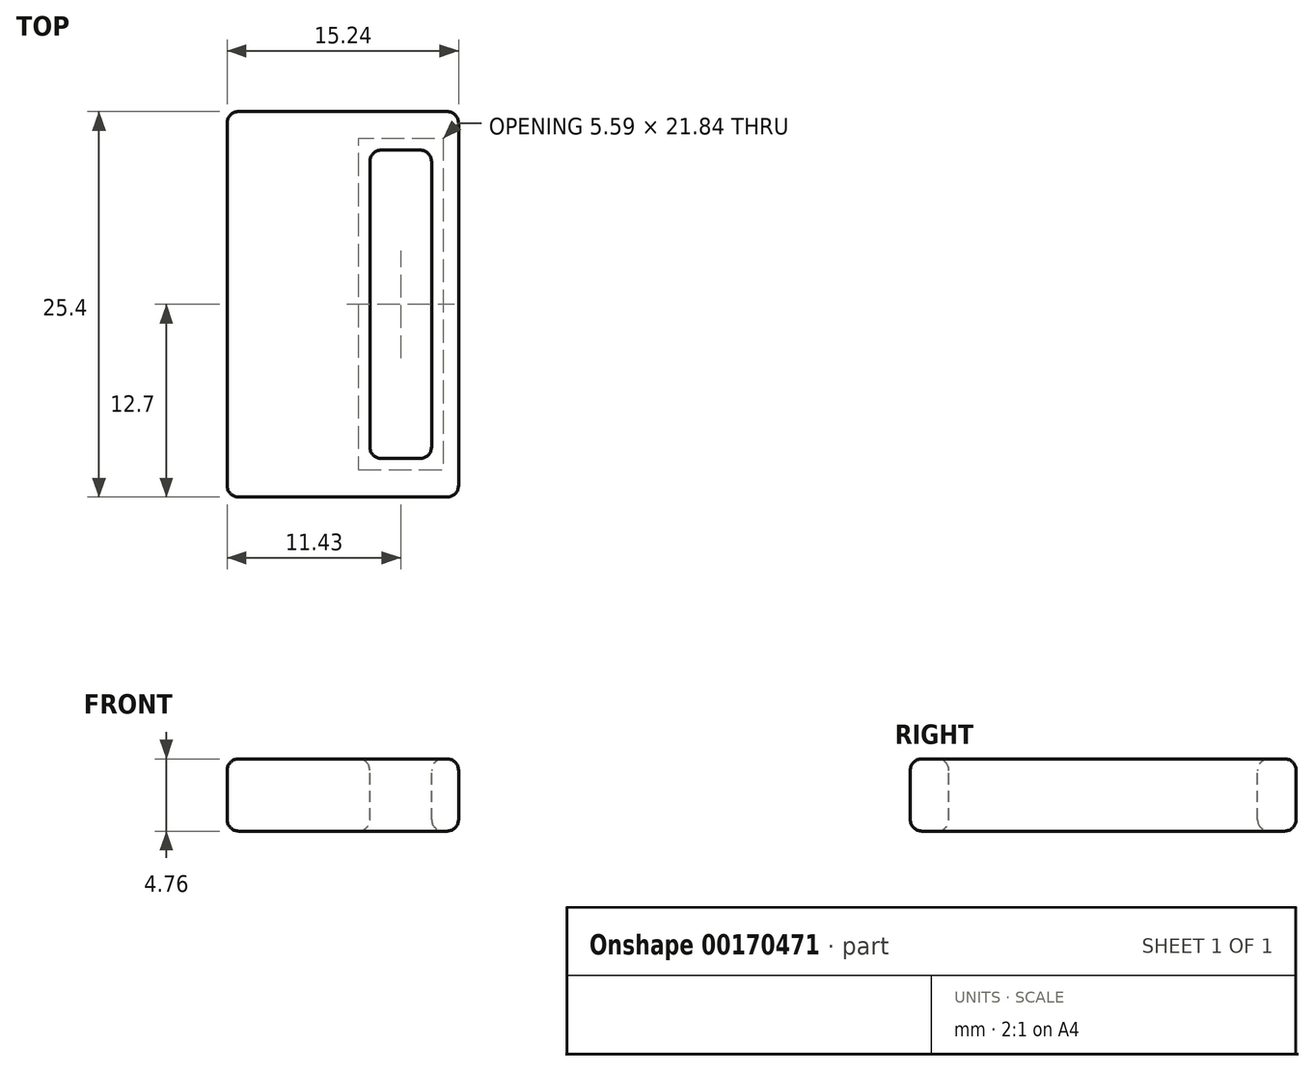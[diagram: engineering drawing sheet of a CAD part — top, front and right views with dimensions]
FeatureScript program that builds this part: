
annotation { "Feature Type Name" : "Feature", "Feature Type Description" : "" }
export const myFeature = defineFeature(function(context is Context, id is Id, definition is map)
    precondition{}
    {
        {
            var Q0;
            Q0=qCreatedBy(makeId("Top.planeOp"),FACE);
            var sketch = newSketch(context, id + "F0", { "sketchPlane" : qUnion([Q0])});
            skLineSegment(sketch, "E0.bottom", {"start": v(7.62, -12.7) * mm, "end": v(-7.62, -12.7) * mm});
            skLineSegment(sketch, "E0.top", {"start": v(7.62, 12.7) * mm, "end": v(-7.62, 12.7) * mm});
            skLineSegment(sketch, "E0.left", {"start": v(7.62, -12.7) * mm, "end": v(7.62, 12.7) * mm});
            skLineSegment(sketch, "E0.right", {"start": v(-7.62, -12.7) * mm, "end": v(-7.62, 12.7) * mm});
            skPoint(sketch, "E0.middle", {"position": v(0, 0) * mm});
            skSolve(sketch);
        }
        {
            var Q0;
            Q0=makeQuery(id+"F0.imprint","IMPRINT",FACE,{"disambiguationData":[TD([[makeQuery(id+"F0.imprint","IMPRINT",EDGE,{"derivedFrom":sQuery(id+"F0.wireOp",EDGE,"E0.bottom")}),-1.0]])]});
            extrude(context, id + "F1", {"entities" : qUnion([Q0]), "depth" : 4.76 * mm});
        }
        {
            var Q0;
            Q0=makeQuery(id+"F1.opExtrude","CAP_FACE",FACE,{"disambiguationData":[OSD([sQuery(id+"F0.wireOp",EDGE,"E0.bottom"),sQuery(id+"F0.wireOp",EDGE,"E0.top"),sQuery(id+"F0.wireOp",EDGE,"E0.left"),sQuery(id+"F0.wireOp",EDGE,"E0.right")])],"isStart":false});
            var sketch = newSketch(context, id + "F2", { "sketchPlane" : qUnion([Q0])});
            skLineSegment(sketch, "E1.bottom", {"start": v(5.84, -10.16) * mm, "end": v(1.78, -10.16) * mm});
            skLineSegment(sketch, "E1.top", {"start": v(5.84, 10.16) * mm, "end": v(1.78, 10.16) * mm});
            skLineSegment(sketch, "E1.left", {"start": v(5.84, -10.16) * mm, "end": v(5.84, 10.16) * mm});
            skLineSegment(sketch, "E1.right", {"start": v(1.78, -10.16) * mm, "end": v(1.78, 10.16) * mm});
            skPoint(sketch, "E1.middle", {"position": v(3.8, 0) * mm});
            skLineSegment(sketch, "E2", {"start": v(0, 0) * mm, "end": v(3.8, 0) * mm, "construction": true});
            skSolve(sketch);
        }
        {
            var Q0;
            Q0=makeQuery(id+"F2.imprint","IMPRINT",FACE,{"disambiguationData":[TD([[makeQuery(id+"F2.imprint","IMPRINT",EDGE,{"derivedFrom":sQuery(id+"F2.wireOp",EDGE,"E1.bottom")}),-1.0]])]});
            extrude(context, id + "F3", {"entities" : qUnion([Q0]), "operationType" : NewBodyOperationType.REMOVE, "oppositeDirection" : true, "depth" : 25.4 * mm});
        }
        {
            var Q0;
            Q0=makeQuery(id+"F1.opExtrude","CAP_FACE",FACE,{"disambiguationData":[OSD([sQuery(id+"F0.wireOp",EDGE,"E0.bottom"),sQuery(id+"F0.wireOp",EDGE,"E0.top"),sQuery(id+"F0.wireOp",EDGE,"E0.left"),sQuery(id+"F0.wireOp",EDGE,"E0.right")])],"isStart":false});
            var Q1;
            Q1=makeQuery(id+"F1.opExtrude","CAP_FACE",FACE,{"disambiguationData":[OSD([sQuery(id+"F0.wireOp",EDGE,"E0.bottom"),sQuery(id+"F0.wireOp",EDGE,"E0.top"),sQuery(id+"F0.wireOp",EDGE,"E0.left"),sQuery(id+"F0.wireOp",EDGE,"E0.right")])],"isStart":true});
            var Q2;
            Q2=makeQuery(id+"F1.opExtrude","SWEPT_FACE",FACE,{"disambiguationData":[OSD([sQuery(id+"F0.wireOp",EDGE,"E0.bottom")])]});
            var Q3;
            Q3=makeQuery(id+"F1.opExtrude","SWEPT_FACE",FACE,{"disambiguationData":[OSD([sQuery(id+"F0.wireOp",EDGE,"E0.left")])]});
            var Q4;
            Q4=makeQuery(id+"F1.opExtrude","SWEPT_FACE",FACE,{"disambiguationData":[OSD([sQuery(id+"F0.wireOp",EDGE,"E0.top")])]});
            var Q5;
            Q5=makeQuery(id+"F3.boolean.opBoolean","COPY",FACE,{"derivedFrom":makeQuery(id+"F3.opExtrude","SWEPT_FACE",FACE,{"disambiguationData":[OSD([sQuery(id+"F2.wireOp",EDGE,"E1.left")])]})});
            var Q6;
            Q6=makeQuery(id+"Fmu9VuXOmDbqxem_1.1.F3.boolean.opBoolean","COPY",FACE,{"derivedFrom":makeQuery(id+"Fmu9VuXOmDbqxem_1.1.F3.opExtrude","SWEPT_FACE",FACE,{"disambiguationData":[OSD([sQuery(id+"F2.wireOp",EDGE,"E1.left")])]})});
            var Q7;
            Q7=makeQuery(id+"Fmu9VuXOmDbqxem_1.1.F3.boolean.opBoolean","COPY",FACE,{"derivedFrom":makeQuery(id+"Fmu9VuXOmDbqxem_1.1.F3.opExtrude","SWEPT_FACE",FACE,{"disambiguationData":[OSD([sQuery(id+"F2.wireOp",EDGE,"E1.right")])]})});
            var Q8;
            Q8=makeQuery(id+"F3.boolean.opBoolean","COPY",FACE,{"derivedFrom":makeQuery(id+"F3.opExtrude","SWEPT_FACE",FACE,{"disambiguationData":[OSD([sQuery(id+"F2.wireOp",EDGE,"E1.right")])]})});
            fillet(context, id + "F4", {"entities" : qUnion([Q0, Q1, Q2, Q3, Q4, Q5, Q6, Q7, Q8]), "radius" : 0.76 * mm, "tangentPropagation" : true, "allowEdgeOverflow" : false});
        }
        {
            var Q0;
            Q0=qCreatedBy(makeId("Front.planeOp"),FACE);
            var sketch = newSketch(context, id + "F5", { "sketchPlane" : qUnion([Q0])});
            skLineSegment(sketch, "E3", {"start": v(4.33, 5.4) * mm, "end": v(4.33, -0.73) * mm});
            skLineSegment(sketch, "E4", {"start": v(3.82, -1.24) * mm, "end": v(-3.5, -1.24) * mm});
            skLineSegment(sketch, "E5", {"start": v(-4.02, -0.73) * mm, "end": v(-4.02, 5.16) * mm});
            skLineSegment(sketch, "E6", {"start": v(-4.52, 5.66) * mm, "end": v(-9.05, 5.66) * mm});
            skLineSegment(sketch, "E7", {"start": v(4.6, 5.67) * mm, "end": v(10.1, 5.67) * mm});
            skPoint(sketch, "E8.visualSharp", {"position": v(4.33, 5.67) * mm});
            skArc(sketch, "E8.filletArc", {"start": v(4.6, 5.67) * mm, "mid": v(4.4, 5.59) * mm, "end": v(4.33, 5.4) * mm});
            skPoint(sketch, "E9.visualSharp", {"position": v(-4.02, 5.66) * mm});
            skArc(sketch, "E9.filletArc", {"start": v(-4.02, 5.16) * mm, "mid": v(-4.16, 5.52) * mm, "end": v(-4.52, 5.66) * mm});
            skPoint(sketch, "E10.visualSharp", {"position": v(-4.02, -1.24) * mm});
            skArc(sketch, "E10.filletArc", {"start": v(-4.02, -0.73) * mm, "mid": v(-3.87, -1.1) * mm, "end": v(-3.5, -1.24) * mm});
            skPoint(sketch, "E11.visualSharp", {"position": v(4.33, -1.24) * mm});
            skArc(sketch, "E11.filletArc", {"start": v(3.82, -1.24) * mm, "mid": v(4.18, -1.1) * mm, "end": v(4.33, -0.73) * mm});
            skSolve(sketch);
        }
        {
            var Q0;
            Q0 = qConstructionFilter(qBodyType(qCreatedBy(id + "F5" ,EDGE), BodyType.WIRE), ConstructionObject.NO);
            extrude(context, id + "F6", {"bodyType" : ToolBodyType.SURFACE, "surfaceEntities" : qUnion([Q0]), "depth" : 20.32 * mm, "symmetric" : true});
        }
    });
